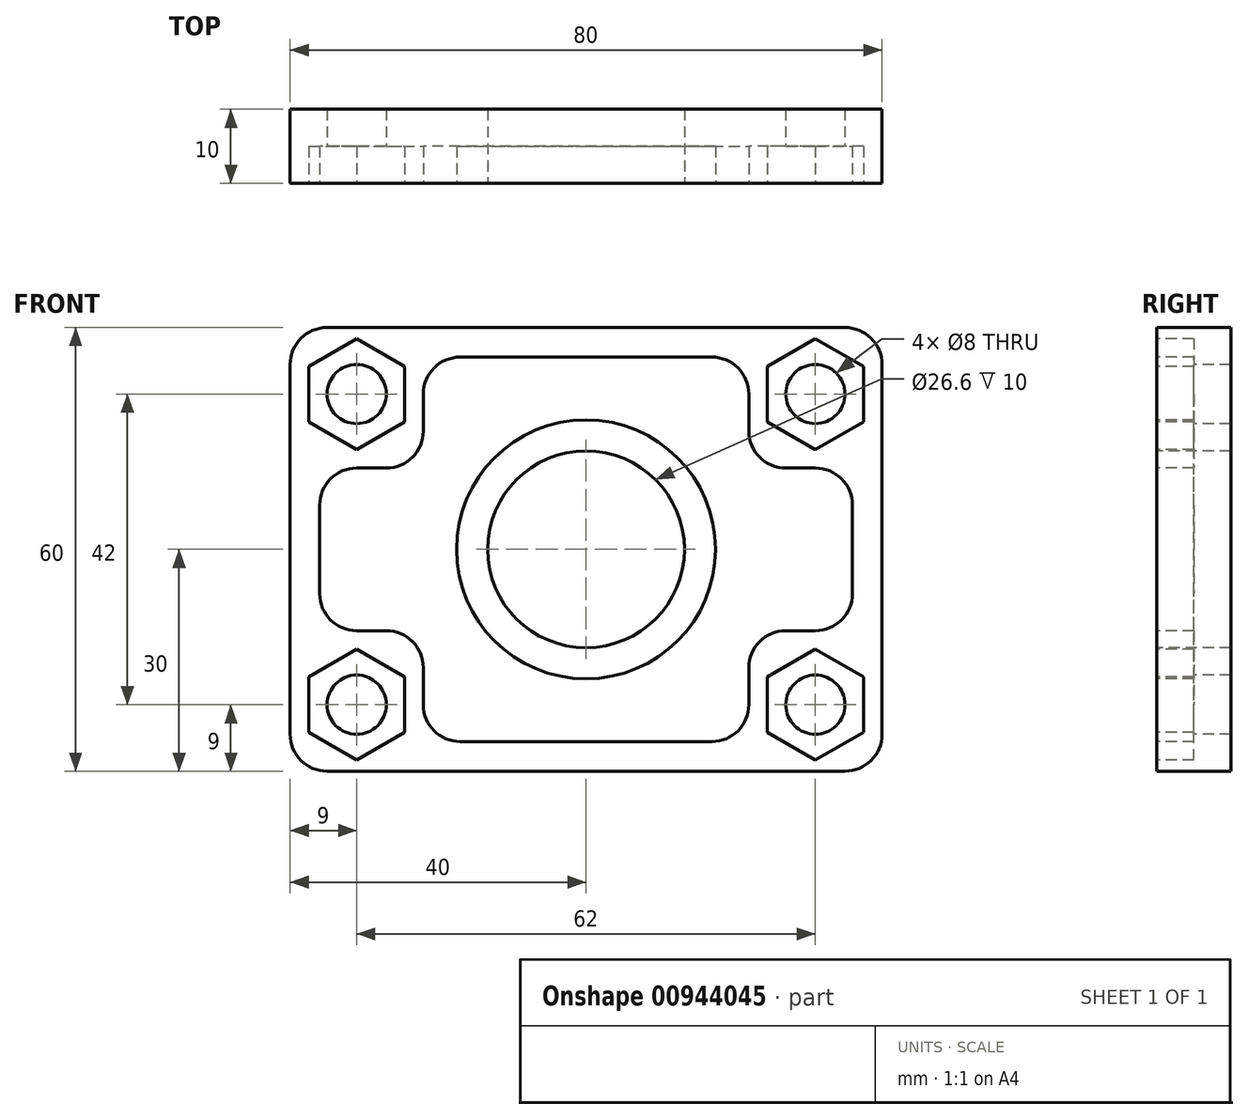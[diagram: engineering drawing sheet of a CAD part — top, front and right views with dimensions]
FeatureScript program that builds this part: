
annotation { "Feature Type Name" : "Feature", "Feature Type Description" : "" }
export const myFeature = defineFeature(function(context is Context, id is Id, definition is map)
    precondition{}
    {
        {
            var Q0;
            Q0=qCreatedBy(makeId("Front.planeOp"),FACE);
            var sketch = newSketch(context, id + "F0", { "sketchPlane" : qUnion([Q0])});
            skLineSegment(sketch, "E0.bottom", {"start": v(-40, 40) * mm, "end": v(40, 40) * mm});
            skLineSegment(sketch, "E0.top", {"start": v(-40, -20) * mm, "end": v(40, -20) * mm});
            skLineSegment(sketch, "E0.left", {"start": v(-40, 40) * mm, "end": v(-40, -20) * mm});
            skLineSegment(sketch, "E0.right", {"start": v(40, 40) * mm, "end": v(40, -20) * mm});
            skSolve(sketch);
        }
        {
            var Q0;
            Q0=qSketchRegion(id+"F0",true);
            extrude(context, id + "F1", {"entities" : qUnion([Q0]), "depth" : 10 * mm, "offsetDistance" : 25 * mm});
        }
        {
            var Q0;
            Q0=makeQuery(id+"F1.opExtrude","CAP_FACE",FACE,{"disambiguationData":[OSD([sQuery(id+"F0.wireOp",EDGE,"E0.bottom"),sQuery(id+"F0.wireOp",EDGE,"E0.top"),sQuery(id+"F0.wireOp",EDGE,"E0.left"),sQuery(id+"F0.wireOp",EDGE,"E0.right")])],"isStart":false});
            var sketch = newSketch(context, id + "F2", { "sketchPlane" : qUnion([Q0])});
            skCircle(sketch, "E1", {"center": v(0, 10) * mm, "radius": 13.3 * mm});
            skSolve(sketch);
        }
        {
            var Q0;
            Q0=qSketchRegion(id+"F2",true);
            extrude(context, id + "F3", {"entities" : qUnion([Q0]), "operationType" : NewBodyOperationType.REMOVE, "endBound" : BoundingType.THROUGH_ALL, "oppositeDirection" : true, "depth" : 25 * mm, "offsetDistance" : 25 * mm});
        }
        {
            var Q0;
            Q0=makeQuery(id+"F1.opExtrude","CAP_FACE",FACE,{"disambiguationData":[OSD([sQuery(id+"F0.wireOp",EDGE,"E0.bottom"),sQuery(id+"F0.wireOp",EDGE,"E0.top"),sQuery(id+"F0.wireOp",EDGE,"E0.left"),sQuery(id+"F0.wireOp",EDGE,"E0.right")])],"isStart":false});
            var sketch = newSketch(context, id + "F4", { "sketchPlane" : qUnion([Q0])});
            skCircle(sketch, "E2", {"center": v(-31, 31) * mm, "radius": 4 * mm});
            skCircle(sketch, "E3", {"center": v(31, 31) * mm, "radius": 4 * mm});
            skCircle(sketch, "E4", {"center": v(-31, -11) * mm, "radius": 4 * mm});
            skCircle(sketch, "E5", {"center": v(31, -11) * mm, "radius": 4 * mm});
            skSolve(sketch);
        }
        {
            var Q0;
            Q0=qSketchRegion(id+"F4",true);
            extrude(context, id + "F5", {"entities" : qUnion([Q0]), "operationType" : NewBodyOperationType.REMOVE, "endBound" : BoundingType.THROUGH_ALL, "oppositeDirection" : true, "depth" : 25 * mm, "offsetDistance" : 25 * mm});
        }
        {
            var Q0;
            Q0=makeQuery(id+"F1.opExtrude","SWEPT_EDGE",EDGE,{"disambiguationData":[OSD([sQuery(id+"F0.wireOp",EDGE,"E0.bottom"),sQuery(id+"F0.wireOp",EDGE,"E0.right")])]});
            var Q1;
            Q1=makeQuery(id+"F1.opExtrude","SWEPT_EDGE",EDGE,{"disambiguationData":[OSD([sQuery(id+"F0.wireOp",EDGE,"E0.top"),sQuery(id+"F0.wireOp",EDGE,"E0.right")])]});
            var Q2;
            Q2=makeQuery(id+"F1.opExtrude","SWEPT_EDGE",EDGE,{"disambiguationData":[OSD([sQuery(id+"F0.wireOp",EDGE,"E0.top"),sQuery(id+"F0.wireOp",EDGE,"E0.left")])]});
            var Q3;
            Q3=makeQuery(id+"F1.opExtrude","SWEPT_EDGE",EDGE,{"disambiguationData":[OSD([sQuery(id+"F0.wireOp",EDGE,"E0.bottom"),sQuery(id+"F0.wireOp",EDGE,"E0.left")])]});
            fillet(context, id + "F6", {"entities" : qUnion([Q0, Q1, Q2, Q3]), "radius" : 5 * mm, "tangentPropagation" : true, "allowEdgeOverflow" : false});
        }
        {
            var Q0;
            Q0=makeQuery(id+"F4.imprint","IMPRINT",FACE,{"disambiguationData":[TD([[makeQuery(id+"F4.imprint","IMPRINT",EDGE,{"derivedFrom":sQuery(id+"F4.wireOp",EDGE,"E2")}),-1.0]])]});
            var sketch = newSketch(context, id + "F7", { "sketchPlane" : qUnion([Q0])});
            skCircle(sketch, "E6.cCircle", {"center": v(-31, 31) * mm, "radius": 6.5 * mm, "construction": true});
            skLineSegment(sketch, "E6.0", {"start": v(-31, 38.5) * mm, "end": v(-24.5, 34.75) * mm});
            skLineSegment(sketch, "E6.1", {"start": v(-24.5, 34.75) * mm, "end": v(-24.5, 27.25) * mm});
            skLineSegment(sketch, "E6.2", {"start": v(-24.5, 27.25) * mm, "end": v(-31, 23.5) * mm});
            skLineSegment(sketch, "E6.3", {"start": v(-31, 23.5) * mm, "end": v(-37.5, 27.25) * mm});
            skLineSegment(sketch, "E6.4", {"start": v(-37.5, 27.25) * mm, "end": v(-37.5, 34.75) * mm});
            skLineSegment(sketch, "E6.5", {"start": v(-37.5, 34.75) * mm, "end": v(-31, 38.5) * mm});
            skPoint(sketch, "E6.0.midPoint", {"position": v(-27.75, 36.63) * mm});
            skCircle(sketch, "E7.cCircle", {"center": v(31, 31) * mm, "radius": 6.5 * mm, "construction": true});
            skLineSegment(sketch, "E7.0", {"start": v(24.5, 27.25) * mm, "end": v(24.5, 34.75) * mm});
            skLineSegment(sketch, "E7.1", {"start": v(24.5, 34.75) * mm, "end": v(31, 38.5) * mm});
            skLineSegment(sketch, "E7.2", {"start": v(31, 38.5) * mm, "end": v(37.5, 34.75) * mm});
            skLineSegment(sketch, "E7.3", {"start": v(37.5, 34.75) * mm, "end": v(37.5, 27.25) * mm});
            skLineSegment(sketch, "E7.4", {"start": v(37.5, 27.25) * mm, "end": v(31, 23.5) * mm});
            skLineSegment(sketch, "E7.5", {"start": v(31, 23.5) * mm, "end": v(24.5, 27.25) * mm});
            skPoint(sketch, "E7.0.midPoint", {"position": v(24.5, 31) * mm});
            skCircle(sketch, "E8.cCircle", {"center": v(31, -11) * mm, "radius": 6.5 * mm, "construction": true});
            skLineSegment(sketch, "E8.0", {"start": v(24.5, -14.75) * mm, "end": v(24.5, -7.25) * mm});
            skLineSegment(sketch, "E8.1", {"start": v(24.5, -7.25) * mm, "end": v(31, -3.5) * mm});
            skLineSegment(sketch, "E8.2", {"start": v(31, -3.5) * mm, "end": v(37.5, -7.25) * mm});
            skLineSegment(sketch, "E8.3", {"start": v(37.5, -7.25) * mm, "end": v(37.5, -14.75) * mm});
            skLineSegment(sketch, "E8.4", {"start": v(37.5, -14.75) * mm, "end": v(31, -18.5) * mm});
            skLineSegment(sketch, "E8.5", {"start": v(31, -18.5) * mm, "end": v(24.5, -14.75) * mm});
            skPoint(sketch, "E8.0.midPoint", {"position": v(24.5, -11) * mm});
            skCircle(sketch, "E9.cCircle", {"center": v(-31, -11) * mm, "radius": 6.5 * mm, "construction": true});
            skLineSegment(sketch, "E9.0", {"start": v(-31, -3.5) * mm, "end": v(-24.5, -7.25) * mm});
            skLineSegment(sketch, "E9.1", {"start": v(-24.5, -7.25) * mm, "end": v(-24.5, -14.75) * mm});
            skLineSegment(sketch, "E9.2", {"start": v(-24.5, -14.75) * mm, "end": v(-31, -18.5) * mm});
            skLineSegment(sketch, "E9.3", {"start": v(-31, -18.5) * mm, "end": v(-37.5, -14.75) * mm});
            skLineSegment(sketch, "E9.4", {"start": v(-37.5, -14.75) * mm, "end": v(-37.5, -7.25) * mm});
            skLineSegment(sketch, "E9.5", {"start": v(-37.5, -7.25) * mm, "end": v(-31, -3.5) * mm});
            skPoint(sketch, "E9.0.midPoint", {"position": v(-27.75, -5.37) * mm});
            skCircle(sketch, "E10", {"center": v(0, 10) * mm, "radius": 17.5 * mm});
            skLineSegment(sketch, "E11.bottom", {"start": v(-22, 36) * mm, "end": v(22, 36) * mm});
            skLineSegment(sketch, "E11.top", {"start": v(-22, -16) * mm, "end": v(22, -16) * mm});
            skLineSegment(sketch, "E11.left", {"start": v(-22, 36) * mm, "end": v(-22, -16) * mm});
            skLineSegment(sketch, "E11.right", {"start": v(22, 36) * mm, "end": v(22, -16) * mm});
            skLineSegment(sketch, "E12.bottom", {"start": v(36, 21) * mm, "end": v(-36, 21) * mm});
            skLineSegment(sketch, "E12.top", {"start": v(36, -1) * mm, "end": v(-36, -1) * mm});
            skLineSegment(sketch, "E12.left", {"start": v(36, 21) * mm, "end": v(36, -1) * mm});
            skLineSegment(sketch, "E12.right", {"start": v(-36, 21) * mm, "end": v(-36, -1) * mm});
            skSolve(sketch);
        }
        {
            var Q0;
            Q0=qSketchRegion(id+"F7",true);
            extrude(context, id + "F8", {"entities" : qUnion([Q0]), "operationType" : NewBodyOperationType.REMOVE, "oppositeDirection" : true, "depth" : 5 * mm, "offsetDistance" : 25 * mm});
        }
        {
            var Q0;
            Q0=makeQuery(id+"F8.boolean.opBoolean","COPY",EDGE,{"derivedFrom":makeQuery(id+"F8.opExtrude","SWEPT_EDGE",EDGE,{"disambiguationData":[OSD([sQuery(id+"F7.wireOp",EDGE,"E11.left"),sQuery(id+"F7.wireOp",EDGE,"E12.bottom")])]})});
            var Q1;
            Q1=makeQuery(id+"F8.boolean.opBoolean","COPY",EDGE,{"derivedFrom":makeQuery(id+"F8.opExtrude","SWEPT_EDGE",EDGE,{"disambiguationData":[OSD([sQuery(id+"F7.wireOp",EDGE,"E12.bottom"),sQuery(id+"F7.wireOp",EDGE,"E12.right")])]})});
            var Q2;
            Q2=makeQuery(id+"F8.boolean.opBoolean","COPY",EDGE,{"derivedFrom":makeQuery(id+"F8.opExtrude","SWEPT_EDGE",EDGE,{"disambiguationData":[OSD([sQuery(id+"F7.wireOp",EDGE,"E11.bottom"),sQuery(id+"F7.wireOp",EDGE,"E11.left")])]})});
            var Q3;
            Q3=makeQuery(id+"F8.boolean.opBoolean","COPY",EDGE,{"derivedFrom":makeQuery(id+"F8.opExtrude","SWEPT_EDGE",EDGE,{"disambiguationData":[OSD([sQuery(id+"F7.wireOp",EDGE,"E11.bottom"),sQuery(id+"F7.wireOp",EDGE,"E11.right")])]})});
            var Q4;
            Q4=makeQuery(id+"F8.boolean.opBoolean","COPY",EDGE,{"derivedFrom":makeQuery(id+"F8.opExtrude","SWEPT_EDGE",EDGE,{"disambiguationData":[OSD([sQuery(id+"F7.wireOp",EDGE,"E11.right"),sQuery(id+"F7.wireOp",EDGE,"E12.bottom")])]})});
            var Q5;
            Q5=makeQuery(id+"F8.boolean.opBoolean","COPY",EDGE,{"derivedFrom":makeQuery(id+"F8.opExtrude","SWEPT_EDGE",EDGE,{"disambiguationData":[OSD([sQuery(id+"F7.wireOp",EDGE,"E12.bottom"),sQuery(id+"F7.wireOp",EDGE,"E12.left")])]})});
            var Q6;
            Q6=makeQuery(id+"F8.boolean.opBoolean","COPY",EDGE,{"derivedFrom":makeQuery(id+"F8.opExtrude","SWEPT_EDGE",EDGE,{"disambiguationData":[OSD([sQuery(id+"F7.wireOp",EDGE,"E12.top"),sQuery(id+"F7.wireOp",EDGE,"E12.right")])]})});
            var Q7;
            Q7=makeQuery(id+"F8.boolean.opBoolean","COPY",EDGE,{"derivedFrom":makeQuery(id+"F8.opExtrude","SWEPT_EDGE",EDGE,{"disambiguationData":[OSD([sQuery(id+"F7.wireOp",EDGE,"E11.left"),sQuery(id+"F7.wireOp",EDGE,"E12.top")])]})});
            var Q8;
            Q8=makeQuery(id+"F8.boolean.opBoolean","COPY",EDGE,{"derivedFrom":makeQuery(id+"F8.opExtrude","SWEPT_EDGE",EDGE,{"disambiguationData":[OSD([sQuery(id+"F7.wireOp",EDGE,"E11.top"),sQuery(id+"F7.wireOp",EDGE,"E11.left")])]})});
            var Q9;
            Q9=makeQuery(id+"F8.boolean.opBoolean","COPY",EDGE,{"derivedFrom":makeQuery(id+"F8.opExtrude","SWEPT_EDGE",EDGE,{"disambiguationData":[OSD([sQuery(id+"F7.wireOp",EDGE,"E12.top"),sQuery(id+"F7.wireOp",EDGE,"E12.left")])]})});
            var Q10;
            Q10=makeQuery(id+"F8.boolean.opBoolean","COPY",EDGE,{"derivedFrom":makeQuery(id+"F8.opExtrude","SWEPT_EDGE",EDGE,{"disambiguationData":[OSD([sQuery(id+"F7.wireOp",EDGE,"E11.right"),sQuery(id+"F7.wireOp",EDGE,"E12.top")])]})});
            var Q11;
            Q11=makeQuery(id+"F8.boolean.opBoolean","COPY",EDGE,{"derivedFrom":makeQuery(id+"F8.opExtrude","SWEPT_EDGE",EDGE,{"disambiguationData":[OSD([sQuery(id+"F7.wireOp",EDGE,"E11.top"),sQuery(id+"F7.wireOp",EDGE,"E11.right")])]})});
            fillet(context, id + "F9", {"entities" : qUnion([Q0, Q1, Q2, Q3, Q4, Q5, Q6, Q7, Q8, Q9, Q10, Q11]), "radius" : 5 * mm, "tangentPropagation" : true, "allowEdgeOverflow" : false});
        }
    });
